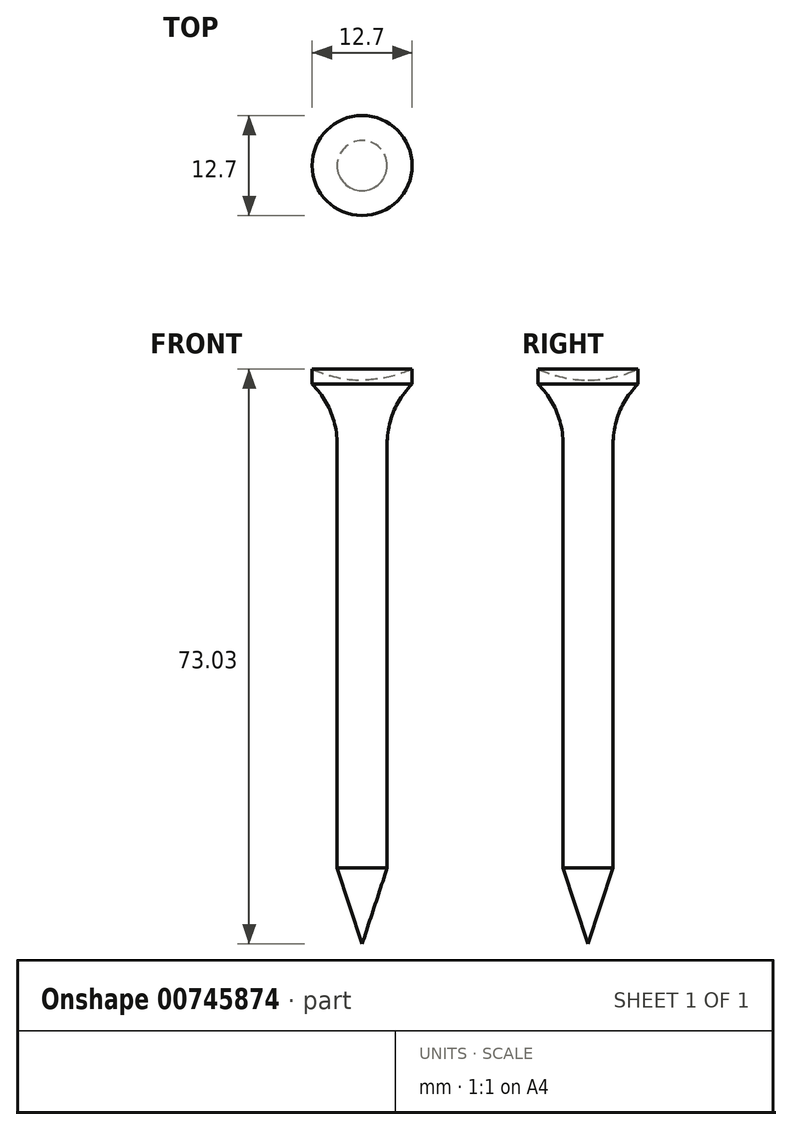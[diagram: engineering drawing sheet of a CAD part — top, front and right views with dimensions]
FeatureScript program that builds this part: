
annotation { "Feature Type Name" : "Feature", "Feature Type Description" : "" }
export const myFeature = defineFeature(function(context is Context, id is Id, definition is map)
    precondition{}
    {
        {
            var Q0;
            Q0=qCreatedBy(makeId("Front.planeOp"),FACE);
            var sketch = newSketch(context, id + "F0", { "sketchPlane" : qUnion([Q0])});
            skLineSegment(sketch, "E0", {"start": v(0, 0) * mm, "end": v(3.17, 9.65) * mm});
            skLineSegment(sketch, "E1", {"start": v(3.17, 9.65) * mm, "end": v(3.17, 63.5) * mm});
            skLineSegment(sketch, "E2", {"start": v(3.17, 63.5) * mm, "end": v(0, 63.5) * mm});
            skLineSegment(sketch, "E3", {"start": v(0, 71.12) * mm, "end": v(0, 0) * mm});
            skArc(sketch, "E4", {"start": v(6.35, 71.12) * mm, "mid": v(4, 67.63) * mm, "end": v(3.18, 63.5) * mm});
            skLineSegment(sketch, "E5", {"start": v(6.35, 71.12) * mm, "end": v(0, 71.12) * mm});
            skLineSegment(sketch, "E6", {"start": v(6.35, 71.12) * mm, "end": v(6.35, 73.03) * mm});
            skArc(sketch, "E7", {"start": v(0, 71.64) * mm, "mid": v(3.25, 71.99) * mm, "end": v(6.35, 73.03) * mm});
            skLineSegment(sketch, "E8", {"start": v(0, 71.12) * mm, "end": v(0, 71.64) * mm});
            skPoint(sketch, "E9.orphan", {"position": v(-6.35, 73.03) * mm});
            skSolve(sketch);
        }
        {
            var Q0;
            Q0=makeQuery(id+"F0.imprint","IMPRINT",FACE,{"disambiguationData":[TD([[makeQuery(id+"F0.imprint","IMPRINT",EDGE,{"derivedFrom":sQuery(id+"F0.wireOp",EDGE,"E5")}),-1.0]])]});
            var Q1;
            {var subQ0=sQuery(id+"F0.wireOp",EDGE,"E2");Q1=makeQuery(id+"F0.imprint","IMPRINT",FACE,{"disambiguationData":[TD([[makeQuery(id+"F0.imprint","IMPRINT",EDGE,{"derivedFrom":subQ0}),-1.0]])]});}
            var Q2;
            {var subQ0=sQuery(id+"F0.wireOp",EDGE,"E0");Q2=makeQuery(id+"F0.imprint","IMPRINT",FACE,{"disambiguationData":[TD([[makeQuery(id+"F0.imprint","IMPRINT",EDGE,{"derivedFrom":subQ0}),1.0]])]});}
            var Q3;
            Q3=sQuery(id+"F0.wireOp",EDGE,"E8");
            revolve(context, id + "F1", {"surfaceOperationType" : NewSurfaceOperationType.NEW, "entities" : qUnion([Q0, Q1, Q2]), "axis" : qUnion([Q3]), "revolveType" : RevolveType.FULL});
        }
    });
